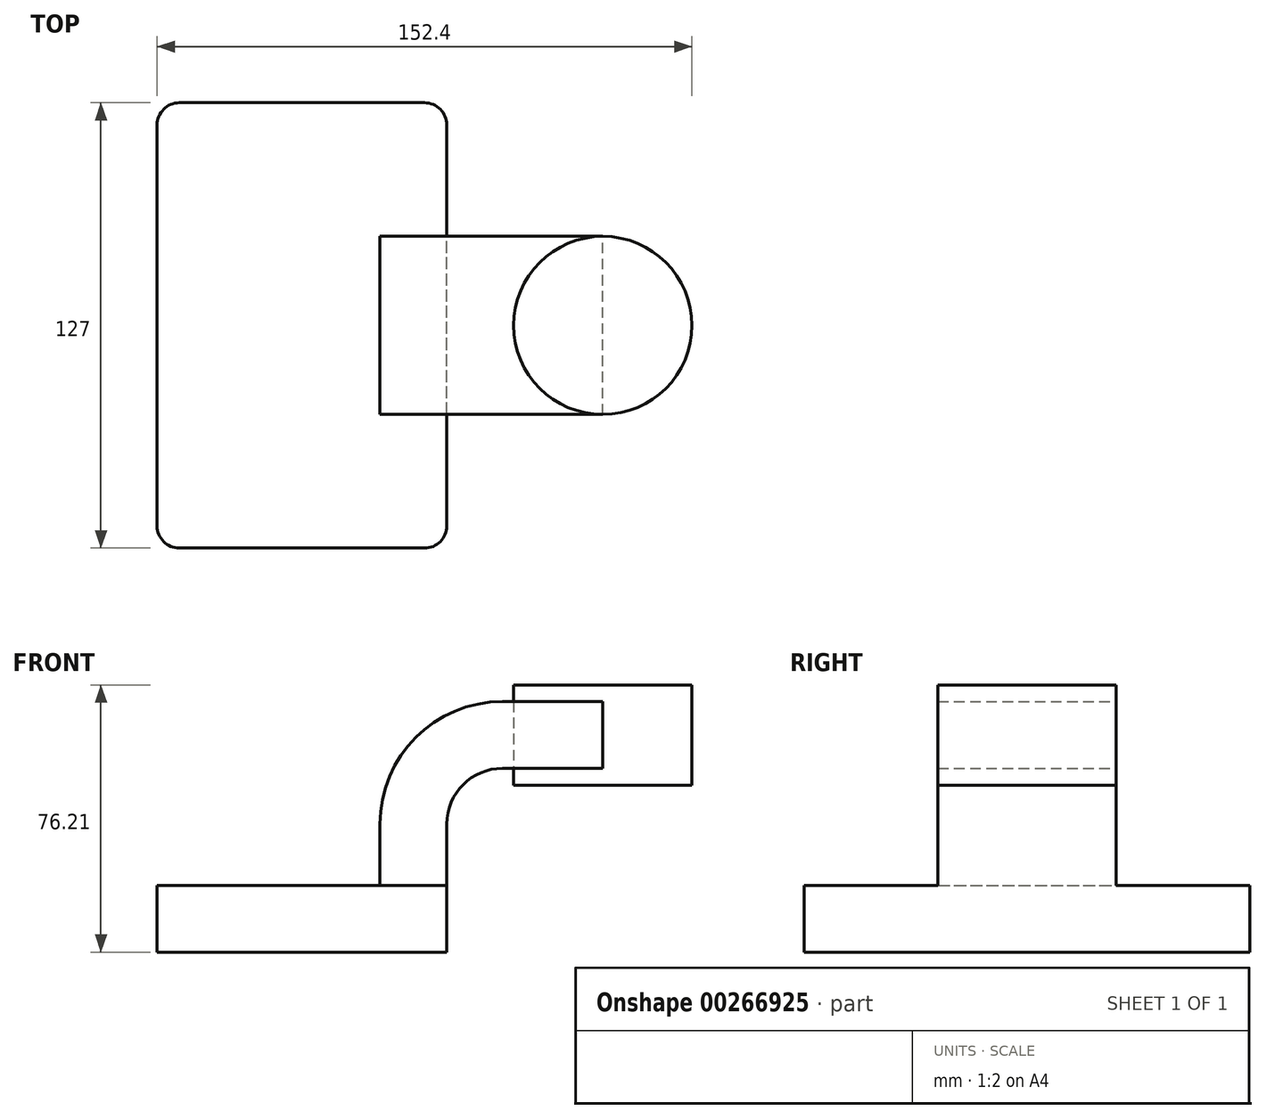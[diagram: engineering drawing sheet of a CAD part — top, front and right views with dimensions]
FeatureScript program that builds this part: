
annotation { "Feature Type Name" : "Feature", "Feature Type Description" : "" }
export const myFeature = defineFeature(function(context is Context, id is Id, definition is map)
    precondition{}
    {
        {
            var Q0;
            Q0=qCreatedBy(makeId("Front.planeOp"),FACE);
            var sketch = newSketch(context, id + "F0", { "sketchPlane" : qUnion([Q0])});
            skLineSegment(sketch, "E0.bottom", {"start": v(-41.27, -9.53) * mm, "end": v(41.28, -9.53) * mm});
            skLineSegment(sketch, "E0.top", {"start": v(-41.28, 9.53) * mm, "end": v(41.28, 9.53) * mm});
            skLineSegment(sketch, "E0.left", {"start": v(-41.28, -9.53) * mm, "end": v(-41.28, 9.53) * mm});
            skLineSegment(sketch, "E0.right", {"start": v(41.28, -9.53) * mm, "end": v(41.28, 9.53) * mm});
            skPoint(sketch, "E0.middle", {"position": v(0, 0) * mm});
            skLineSegment(sketch, "E1.bottom", {"start": v(111.12, 38.1) * mm, "end": v(60.33, 38.1) * mm});
            skLineSegment(sketch, "E1.top", {"start": v(111.13, 66.68) * mm, "end": v(60.33, 66.68) * mm});
            skLineSegment(sketch, "E1.left", {"start": v(111.13, 38.1) * mm, "end": v(111.13, 66.68) * mm});
            skLineSegment(sketch, "E1.right", {"start": v(60.33, 38.1) * mm, "end": v(60.33, 66.68) * mm});
            skPoint(sketch, "E1.middle", {"position": v(85.73, 52.39) * mm});
            skLineSegment(sketch, "E2", {"start": v(41.27, 9.53) * mm, "end": v(41.27, 27) * mm});
            skArc(sketch, "E3", {"start": v(41.27, 27) * mm, "mid": v(45.92, 38.23) * mm, "end": v(57.15, 42.88) * mm});
            skLineSegment(sketch, "E4", {"start": v(57.15, 42.88) * mm, "end": v(85.73, 42.88) * mm});
            skLineSegment(sketch, "E5.0", {"start": v(57.15, 61.93) * mm, "end": v(85.73, 61.93) * mm});
            skArc(sketch, "E5.1", {"start": v(22.22, 27) * mm, "mid": v(32.45, 51.7) * mm, "end": v(57.15, 61.93) * mm});
            skLineSegment(sketch, "E5.2", {"start": v(22.22, 9.53) * mm, "end": v(22.22, 27) * mm});
            skFitSpline(sketch, "E6", {"points": [v(-41.27, 9.53) * mm, v(57.15, 61.93) * mm], "startDerivative": vector(159.4, 67.2) * mm, "endDerivative": vector(151, -5.23) * mm});
            skLineSegment(sketch, "E7", {"start": v(85.73, 38.1) * mm, "end": v(85.73, 66.68) * mm});
            skSolve(sketch);
        }
        {
            var Q0;
            Q0=makeQuery(id+"F0.imprint","IMPRINT",FACE,{"disambiguationData":[TD([[makeQuery(id+"F0.imprint","IMPRINT",EDGE,{"derivedFrom":sQuery(id+"F0.wireOp",EDGE,"E0.bottom")}),1.0]])]});
            extrude(context, id + "F1", {"entities" : qUnion([Q0]), "endBound" : BoundingType.SYMMETRIC, "depth" : 127 * mm});
        }
        {
            var Q0;
            {var subQ2=sQuery(id+"F0.wireOp",EDGE,"E2");Q0=makeQuery(id+"F0.imprint","IMPRINT",FACE,{"disambiguationData":[TD([[makeQuery(id+"F0.imprint","IMPRINT",EDGE,{"derivedFrom":subQ2}),1.0]])]});}
            var Q1;
            {var subQ0=sQuery(id+"F0.wireOp",EDGE,"E4");var subQ1=sQuery(id+"F0.wireOp",EDGE,"E1.right");var subQ2=makeQuery(id+"F0.imprint","INTERSECT",VERTEX,{"derivedFrom":[subQ1,subQ0]});Q1=makeQuery(id+"F0.imprint","IMPRINT",FACE,{"disambiguationData":[TD([[makeQuery(id+"F0.imprint","IMPRINT",EDGE,{"disambiguationData":[TD([[subQ2,-1.0]])],"derivedFrom":subQ1}),-1.0]])]});}
            extrude(context, id + "F2", {"entities" : qUnion([Q0, Q1]), "operationType" : NewBodyOperationType.ADD, "endBound" : BoundingType.SYMMETRIC, "depth" : 50.8 * mm});
        }
        {
            var Q0;
            Q0=makeQuery(id+"F0.imprint","IMPRINT",FACE,{"disambiguationData":[TD([[makeQuery(id+"F0.imprint","IMPRINT",EDGE,{"derivedFrom":sQuery(id+"F0.wireOp",EDGE,"E5.1")}),1.0]])]});
            extrude(context, id + "F3", {"entities" : qUnion([Q0]), "operationType" : NewBodyOperationType.ADD, "endBound" : BoundingType.SYMMETRIC, "depth" : 15.88 * mm});
        }
        {
            var Q0;
            {var subQ0=sQuery(id+"F0.wireOp",EDGE,"E1.left");Q0=makeQuery(id+"F0.imprint","IMPRINT",FACE,{"disambiguationData":[TD([[makeQuery(id+"F0.imprint","IMPRINT",EDGE,{"derivedFrom":subQ0}),1.0]])]});}
            var Q1;
            Q1=sQuery(id+"F0.wireOp",EDGE,"E7");
            revolve(context, id + "F4", {"entities" : qUnion([Q0]), "axis" : qUnion([Q1]), "revolveType" : RevolveType.FULL});
        }
        {
            var Q0;
            Q0=makeQuery(id+"F1.opExtrude","CAP_EDGE",EDGE,{"disambiguationData":[OSD([sQuery(id+"F0.wireOp",EDGE,"E0.right")])],"isStart":false});
            var Q1;
            Q1=makeQuery(id+"F1.opExtrude","CAP_EDGE",EDGE,{"disambiguationData":[OSD([sQuery(id+"F0.wireOp",EDGE,"E0.left")])],"isStart":false});
            var Q2;
            Q2=makeQuery(id+"F1.opExtrude","CAP_EDGE",EDGE,{"disambiguationData":[OSD([sQuery(id+"F0.wireOp",EDGE,"E0.right")])],"isStart":true});
            var Q3;
            Q3=makeQuery(id+"F1.opExtrude","CAP_EDGE",EDGE,{"disambiguationData":[OSD([sQuery(id+"F0.wireOp",EDGE,"E0.left")])],"isStart":true});
            fillet(context, id + "F5", {"entities" : qUnion([Q0, Q1, Q2, Q3]), "radius" : 6.35 * mm, "tangentPropagation" : true, "allowEdgeOverflow" : false});
        }
    });
